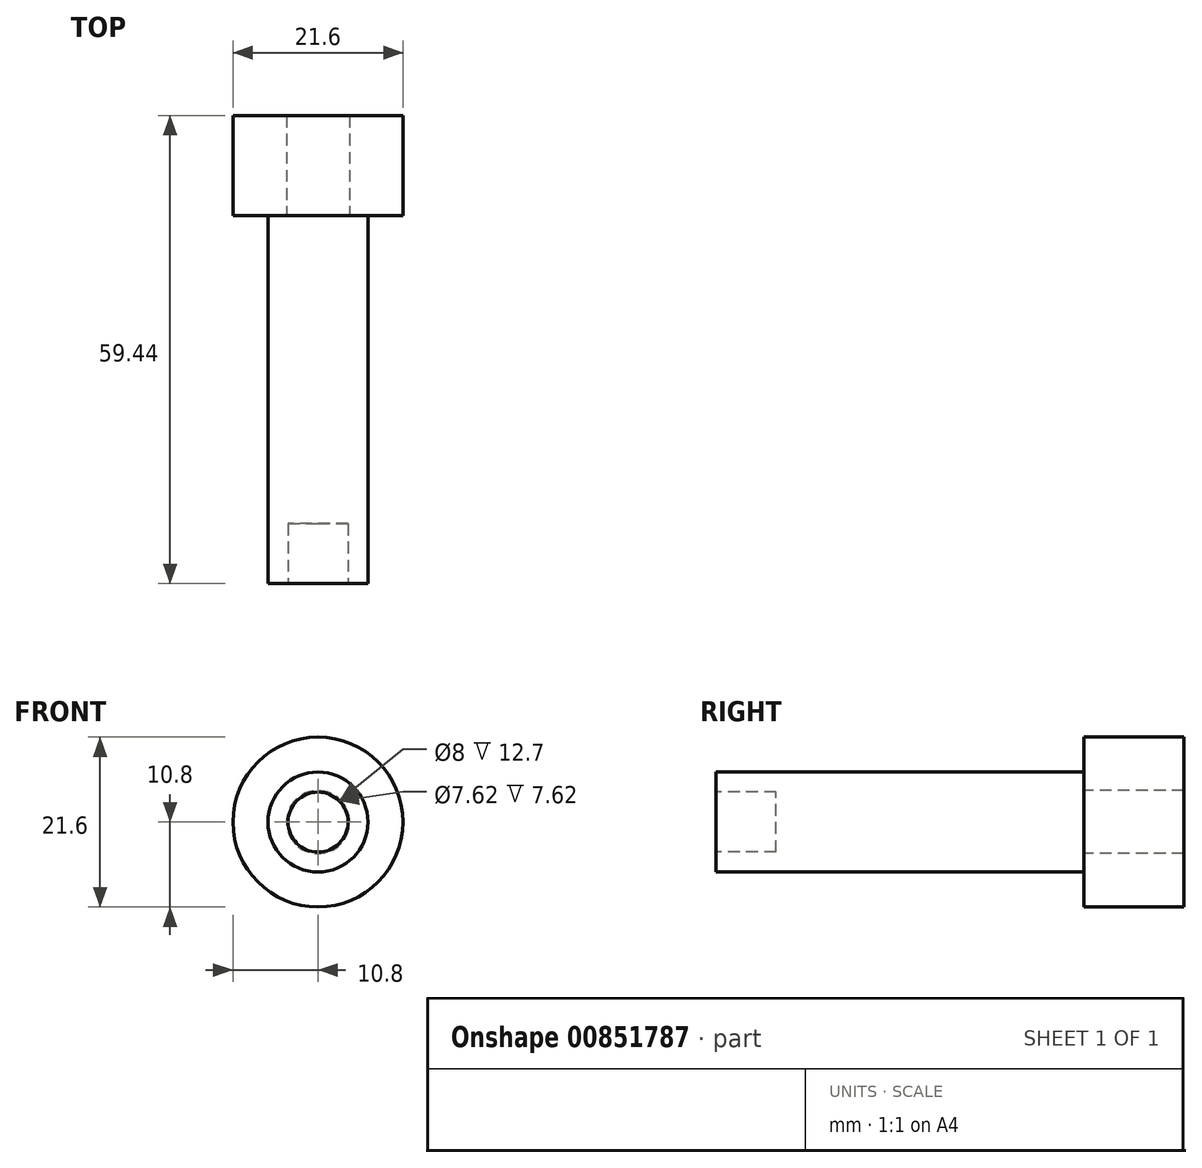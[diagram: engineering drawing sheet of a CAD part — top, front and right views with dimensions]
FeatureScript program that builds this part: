
annotation { "Feature Type Name" : "Feature", "Feature Type Description" : "" }
export const myFeature = defineFeature(function(context is Context, id is Id, definition is map)
    precondition{}
    {
        {
            var Q0;
            Q0=qCreatedBy(makeId("Front.planeOp"),FACE);
            var sketch = newSketch(context, id + "F0", { "sketchPlane" : qUnion([Q0])});
            skCircle(sketch, "E0", {"center": v(0, 0) * mm, "radius": 6.35 * mm});
            skSolve(sketch);
        }
        {
            var Q0;
            Q0 = qSketchRegion(id + "F0", true);
            extrude(context, id + "F1", {"entities" : qUnion([Q0]), "depth" : 46.74 * mm, "offsetDistance" : 25.4 * mm});
        }
        {
            var Q0;
            Q0=qCreatedBy(makeId("Front.planeOp"),FACE);
            var sketch = newSketch(context, id + "F2", { "sketchPlane" : qUnion([Q0])});
            skCircle(sketch, "E1", {"center": v(0, 0) * mm, "radius": 10.8 * mm});
            skCircle(sketch, "E2", {"center": v(0, 0) * mm, "radius": 4 * mm});
            skSolve(sketch);
        }
        {
            var Q0;
            Q0 = qSketchRegion(id + "F2", true);
            extrude(context, id + "F3", {"entities" : qUnion([Q0]), "operationType" : NewBodyOperationType.ADD, "oppositeDirection" : true, "depth" : 12.7 * mm, "offsetDistance" : 25.4 * mm});
        }
        {
            var Q0;
            Q0=makeQuery(id+"F1.opExtrude","CAP_FACE",FACE,{"disambiguationData":[OSD([sQuery(id+"F0.wireOp",EDGE,"E0")])],"isStart":false});
            var sketch = newSketch(context, id + "F4", { "sketchPlane" : qUnion([Q0])});
            skCircle(sketch, "E3", {"center": v(0, 0) * mm, "radius": 3.8 * mm});
            skSolve(sketch);
        }
        {
            var Q0;
            Q0=makeQuery(id+"F4.imprint","IMPRINT",FACE,{"disambiguationData":[TD([[makeQuery(id+"F4.imprint","IMPRINT",EDGE,{"derivedFrom":sQuery(id+"F4.wireOp",EDGE,"E3")}),1.0]])]});
            extrude(context, id + "F5", {"entities" : qUnion([Q0]), "operationType" : NewBodyOperationType.REMOVE, "oppositeDirection" : true, "depth" : 7.62 * mm, "offsetDistance" : 25.4 * mm});
        }
    });
